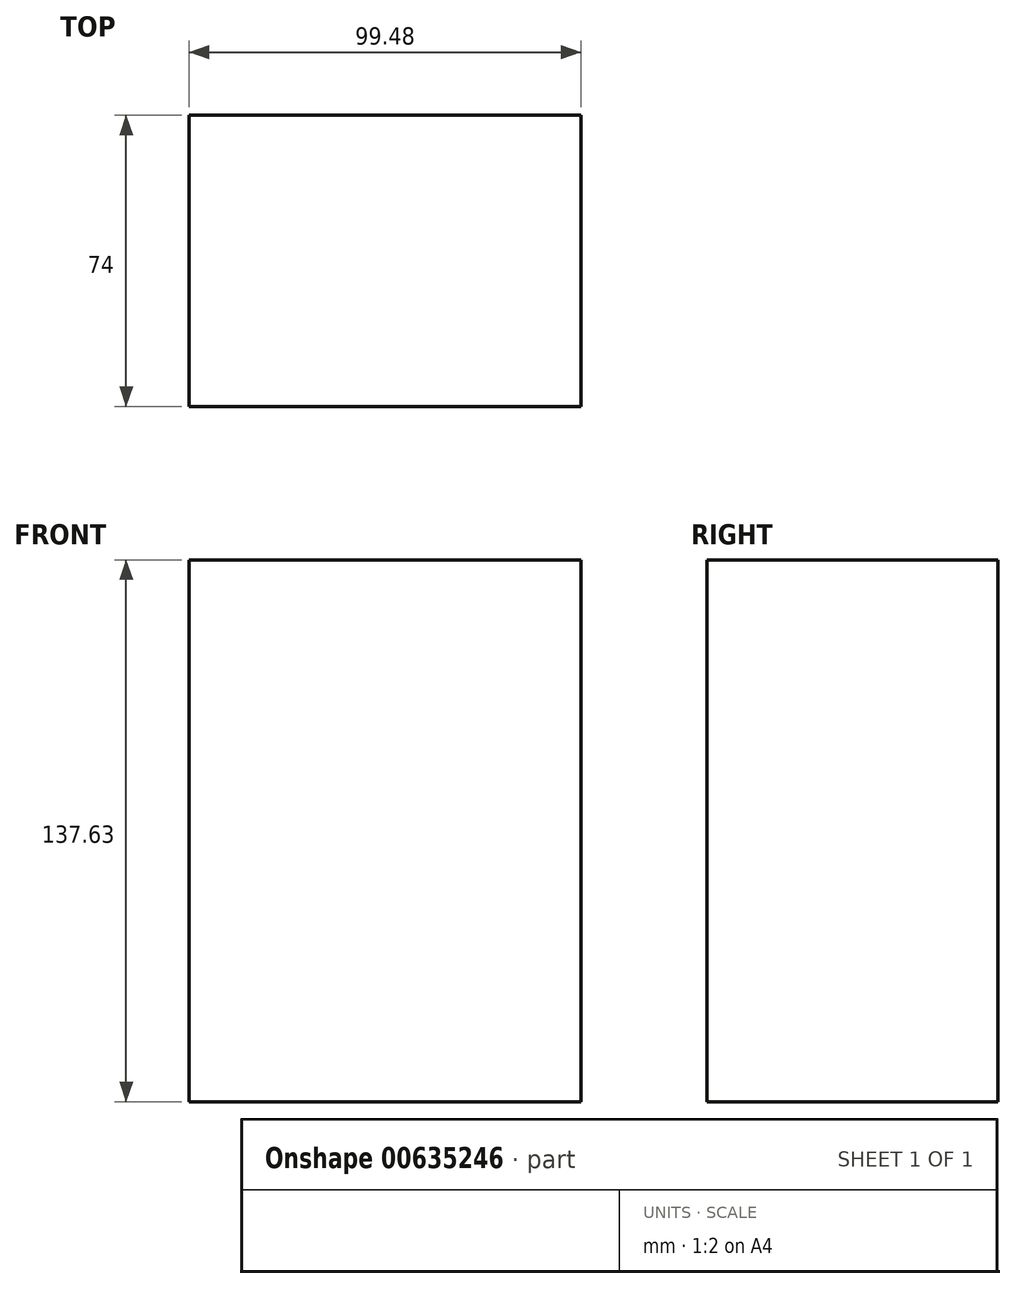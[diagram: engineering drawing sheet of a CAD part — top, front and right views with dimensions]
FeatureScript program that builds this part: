
annotation { "Feature Type Name" : "Feature", "Feature Type Description" : "" }
export const myFeature = defineFeature(function(context is Context, id is Id, definition is map)
    precondition{}
    {
        {
            var Q0;
            Q0=qCreatedBy(makeId("Top.planeOp"),FACE);
            var sketch = newSketch(context, id + "F0", { "sketchPlane" : qUnion([Q0])});
            skLineSegment(sketch, "E0.bottom", {"start": v(-46.4, 22.71) * mm, "end": v(53.08, 22.71) * mm});
            skLineSegment(sketch, "E0.top", {"start": v(-46.4, -51.29) * mm, "end": v(53.08, -51.29) * mm});
            skLineSegment(sketch, "E0.left", {"start": v(-46.4, 22.71) * mm, "end": v(-46.4, -51.29) * mm});
            skLineSegment(sketch, "E0.right", {"start": v(53.08, 22.71) * mm, "end": v(53.08, -51.29) * mm});
            skSolve(sketch);
        }
        {
            var Q0;
            Q0 = qSketchRegion(id + "F0", true);
            extrude(context, id + "F1", {"entities" : qUnion([Q0]), "depth" : 137.63 * mm, "offsetDistance" : 25.4 * mm});
        }
    });
